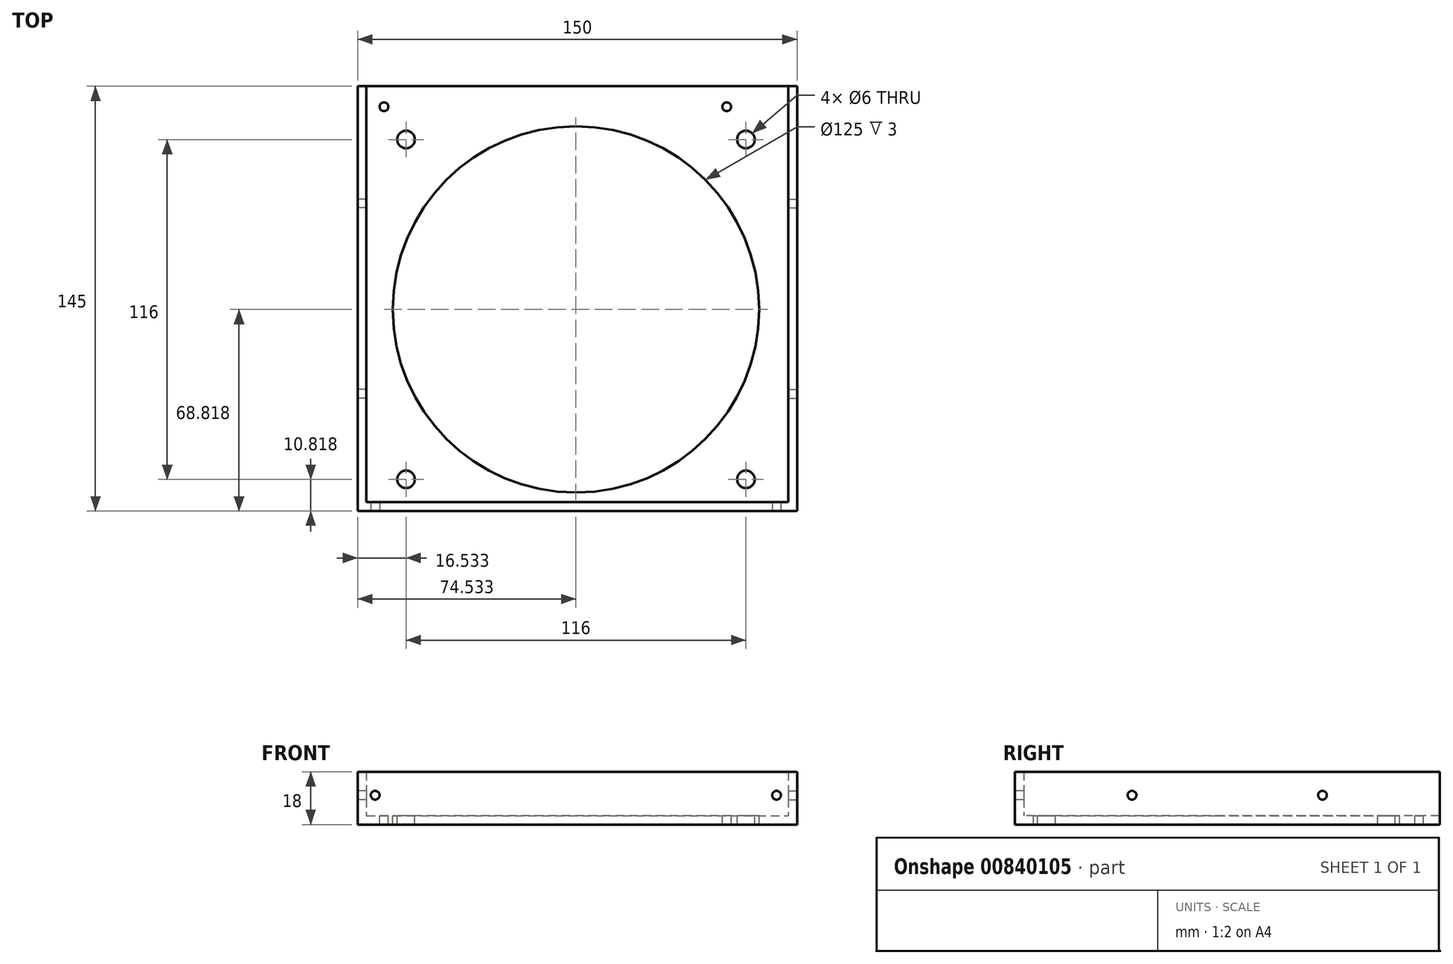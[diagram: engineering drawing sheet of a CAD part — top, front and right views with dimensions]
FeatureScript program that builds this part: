
annotation { "Feature Type Name" : "Feature", "Feature Type Description" : "" }
export const myFeature = defineFeature(function(context is Context, id is Id, definition is map)
    precondition{}
    {
        {
            var Q0;
            Q0=qCreatedBy(makeId("Top.planeOp"),FACE);
            var sketch = newSketch(context, id + "F0", { "sketchPlane" : qUnion([Q0])});
            skLineSegment(sketch, "E0.bottom", {"start": v(-58.92, 79.83) * mm, "end": v(91.08, 79.83) * mm});
            skLineSegment(sketch, "E0.top", {"start": v(-58.92, -65.17) * mm, "end": v(91.08, -65.17) * mm});
            skLineSegment(sketch, "E0.left", {"start": v(-58.92, 79.83) * mm, "end": v(-58.92, -65.17) * mm});
            skLineSegment(sketch, "E0.right", {"start": v(91.08, 79.83) * mm, "end": v(91.08, -65.17) * mm});
            skLineSegment(sketch, "E1", {"start": v(91.08, 79.83) * mm, "end": v(67.08, 79.83) * mm, "construction": true});
            skLineSegment(sketch, "E2", {"start": v(67.08, 79.83) * mm, "end": v(67.08, 72.83) * mm, "construction": true});
            skCircle(sketch, "E3", {"center": v(67.08, 72.83) * mm, "radius": 1.5 * mm});
            skLineSegment(sketch, "E4", {"start": v(-58.92, 79.83) * mm, "end": v(-49.92, 79.83) * mm, "construction": true});
            skLineSegment(sketch, "E5", {"start": v(-49.92, 79.83) * mm, "end": v(-49.92, 63.94) * mm, "construction": true});
            skCircle(sketch, "E6", {"center": v(-49.92, 72.83) * mm, "radius": 1.5 * mm});
            skLineSegment(sketch, "E7.bottom", {"start": v(-42.39, 61.65) * mm, "end": v(73.61, 61.65) * mm, "construction": true});
            skLineSegment(sketch, "E7.top", {"start": v(-42.39, -54.35) * mm, "end": v(73.61, -54.35) * mm, "construction": true});
            skLineSegment(sketch, "E7.left", {"start": v(-42.39, 61.65) * mm, "end": v(-42.39, -54.35) * mm, "construction": true});
            skLineSegment(sketch, "E7.right", {"start": v(73.61, 61.65) * mm, "end": v(73.61, -54.35) * mm, "construction": true});
            skLineSegment(sketch, "E8", {"start": v(-42.39, 61.65) * mm, "end": v(73.61, -54.35) * mm, "construction": true});
            skCircle(sketch, "E9", {"center": v(15.61, 3.65) * mm, "radius": 62.5 * mm});
            skCircle(sketch, "E10", {"center": v(-42.39, 61.65) * mm, "radius": 3 * mm});
            skCircle(sketch, "E11", {"center": v(-42.39, -54.35) * mm, "radius": 3 * mm});
            skCircle(sketch, "E12", {"center": v(73.61, -54.35) * mm, "radius": 3 * mm});
            skCircle(sketch, "E13", {"center": v(73.61, 61.65) * mm, "radius": 3 * mm});
            skLineSegment(sketch, "E14", {"start": v(-228.5, -70.16) * mm, "end": v(-428.5, -70.16) * mm});
            skLineSegment(sketch, "E15", {"start": v(-428.5, -70.16) * mm, "end": v(-428.5, 129.84) * mm});
            skLineSegment(sketch, "E16", {"start": v(-428.5, 129.84) * mm, "end": v(-228.5, -70.16) * mm});
            skLineSegment(sketch, "E17", {"start": v(-428.5, -70.16) * mm, "end": v(-425.5, -70.16) * mm});
            skLineSegment(sketch, "E18", {"start": v(-425.5, -70.16) * mm, "end": v(-425.5, 126.84) * mm});
            skLineSegment(sketch, "E19", {"start": v(-428.5, -70.16) * mm, "end": v(-428.5, -67.16) * mm});
            skLineSegment(sketch, "E20", {"start": v(-428.5, -67.16) * mm, "end": v(-231.5, -67.16) * mm});
            skLineSegment(sketch, "E21", {"start": v(-228.5, -70.16) * mm, "end": v(-232.75, -70.16) * mm});
            skLineSegment(sketch, "E22", {"start": v(-232.75, -70.16) * mm, "end": v(-428.5, 125.6) * mm});
            skLineSegment(sketch, "E23", {"start": v(-428.5, -70.16) * mm, "end": v(-330.63, 27.72) * mm});
            skLineSegment(sketch, "E24", {"start": v(-428.5, -67.16) * mm, "end": v(-332.13, 29.22) * mm});
            skLineSegment(sketch, "E25", {"start": v(-425.5, -70.16) * mm, "end": v(-329.13, 26.22) * mm});
            skLineSegment(sketch, "E26", {"start": v(-58.92, 79.83) * mm, "end": v(-55.92, 79.83) * mm, "construction": true});
            skLineSegment(sketch, "E27", {"start": v(-55.92, 79.83) * mm, "end": v(-55.92, -65.17) * mm});
            skLineSegment(sketch, "E28", {"start": v(-58.92, -65.17) * mm, "end": v(-58.92, -62.17) * mm, "construction": true});
            skLineSegment(sketch, "E29", {"start": v(-58.92, -62.17) * mm, "end": v(91.08, -62.17) * mm});
            skLineSegment(sketch, "E30", {"start": v(91.08, -65.17) * mm, "end": v(88.08, -65.17) * mm, "construction": true});
            skLineSegment(sketch, "E31", {"start": v(88.08, -65.17) * mm, "end": v(88.08, 79.83) * mm});
            skLineSegment(sketch, "E32", {"start": v(67.08, 72.83) * mm, "end": v(-65.04, 72.83) * mm, "construction": true});
            skSolve(sketch);
        }
        {
            var Q0;
            {var subQ0=sQuery(id+"F0.wireOp",EDGE,"E0.left");var subQ1=sQuery(id+"F0.wireOp",EDGE,"E0.bottom");var subQ2=makeQuery(id+"F0.imprint","INTERSECT",VERTEX,{"derivedFrom":[subQ1,subQ0]});Q0=makeQuery(id+"F0.imprint","IMPRINT",FACE,{"disambiguationData":[TD([[makeQuery(id+"F0.imprint","IMPRINT",EDGE,{"disambiguationData":[TD([[subQ2,-1.0]])],"derivedFrom":subQ1}),-1.0]])]});}
            var Q1;
            Q1=makeQuery(id+"F0.imprint","IMPRINT",FACE,{"disambiguationData":[TD([[makeQuery(id+"F0.imprint","IMPRINT",EDGE,{"derivedFrom":sQuery(id+"F0.wireOp",EDGE,"E3")}),-1.0]])]});
            var Q2;
            {var subQ0=sQuery(id+"F0.wireOp",EDGE,"E0.right");var subQ1=sQuery(id+"F0.wireOp",EDGE,"E0.bottom");var subQ2=makeQuery(id+"F0.imprint","INTERSECT",VERTEX,{"derivedFrom":[subQ1,subQ0]});Q2=makeQuery(id+"F0.imprint","IMPRINT",FACE,{"disambiguationData":[TD([[makeQuery(id+"F0.imprint","IMPRINT",EDGE,{"disambiguationData":[TD([[subQ2,1.0]])],"derivedFrom":subQ1}),-1.0]])]});}
            var Q3;
            {var subQ0=sQuery(id+"F0.wireOp",EDGE,"E27");var subQ1=sQuery(id+"F0.wireOp",EDGE,"E0.top");var subQ2=makeQuery(id+"F0.imprint","INTERSECT",VERTEX,{"derivedFrom":[subQ1,subQ0]});Q3=makeQuery(id+"F0.imprint","IMPRINT",FACE,{"disambiguationData":[TD([[makeQuery(id+"F0.imprint","IMPRINT",EDGE,{"disambiguationData":[TD([[subQ2,-1.0]])],"derivedFrom":subQ1}),1.0]])]});}
            var Q4;
            {var subQ0=sQuery(id+"F0.wireOp",EDGE,"E0.right");var subQ1=sQuery(id+"F0.wireOp",EDGE,"E0.top");var subQ2=makeQuery(id+"F0.imprint","INTERSECT",VERTEX,{"derivedFrom":[subQ1,subQ0]});Q4=makeQuery(id+"F0.imprint","IMPRINT",FACE,{"disambiguationData":[TD([[makeQuery(id+"F0.imprint","IMPRINT",EDGE,{"disambiguationData":[TD([[subQ2,1.0]])],"derivedFrom":subQ1}),1.0]])]});}
            var Q5;
            {var subQ0=sQuery(id+"F0.wireOp",EDGE,"E0.left");var subQ1=sQuery(id+"F0.wireOp",EDGE,"E0.top");var subQ2=makeQuery(id+"F0.imprint","INTERSECT",VERTEX,{"derivedFrom":[subQ1,subQ0]});Q5=makeQuery(id+"F0.imprint","IMPRINT",FACE,{"disambiguationData":[TD([[makeQuery(id+"F0.imprint","IMPRINT",EDGE,{"disambiguationData":[TD([[subQ2,-1.0]])],"derivedFrom":subQ1}),1.0]])]});}
            extrude(context, id + "F1", {"entities" : qUnion([Q0, Q1, Q2, Q3, Q4, Q5]), "oppositeDirection" : true, "depth" : 3 * mm, "offsetDistance" : 25 * mm});
        }
        {
            var Q0;
            {var subQ0=sQuery(id+"F0.wireOp",EDGE,"E0.left");var subQ1=sQuery(id+"F0.wireOp",EDGE,"E0.bottom");var subQ2=makeQuery(id+"F0.imprint","INTERSECT",VERTEX,{"derivedFrom":[subQ1,subQ0]});Q0=makeQuery(id+"F0.imprint","IMPRINT",FACE,{"disambiguationData":[TD([[makeQuery(id+"F0.imprint","IMPRINT",EDGE,{"disambiguationData":[TD([[subQ2,-1.0]])],"derivedFrom":subQ1}),-1.0]])]});}
            var Q1;
            {var subQ0=sQuery(id+"F0.wireOp",EDGE,"E0.left");var subQ1=sQuery(id+"F0.wireOp",EDGE,"E0.top");var subQ2=makeQuery(id+"F0.imprint","INTERSECT",VERTEX,{"derivedFrom":[subQ1,subQ0]});Q1=makeQuery(id+"F0.imprint","IMPRINT",FACE,{"disambiguationData":[TD([[makeQuery(id+"F0.imprint","IMPRINT",EDGE,{"disambiguationData":[TD([[subQ2,-1.0]])],"derivedFrom":subQ1}),1.0]])]});}
            var Q2;
            {var subQ0=sQuery(id+"F0.wireOp",EDGE,"E27");var subQ1=sQuery(id+"F0.wireOp",EDGE,"E0.top");var subQ2=makeQuery(id+"F0.imprint","INTERSECT",VERTEX,{"derivedFrom":[subQ1,subQ0]});Q2=makeQuery(id+"F0.imprint","IMPRINT",FACE,{"disambiguationData":[TD([[makeQuery(id+"F0.imprint","IMPRINT",EDGE,{"disambiguationData":[TD([[subQ2,-1.0]])],"derivedFrom":subQ1}),1.0]])]});}
            var Q3;
            {var subQ0=sQuery(id+"F0.wireOp",EDGE,"E0.right");var subQ1=sQuery(id+"F0.wireOp",EDGE,"E0.top");var subQ2=makeQuery(id+"F0.imprint","INTERSECT",VERTEX,{"derivedFrom":[subQ1,subQ0]});Q3=makeQuery(id+"F0.imprint","IMPRINT",FACE,{"disambiguationData":[TD([[makeQuery(id+"F0.imprint","IMPRINT",EDGE,{"disambiguationData":[TD([[subQ2,1.0]])],"derivedFrom":subQ1}),1.0]])]});}
            var Q4;
            {var subQ0=sQuery(id+"F0.wireOp",EDGE,"E0.right");var subQ1=sQuery(id+"F0.wireOp",EDGE,"E0.bottom");var subQ2=makeQuery(id+"F0.imprint","INTERSECT",VERTEX,{"derivedFrom":[subQ1,subQ0]});Q4=makeQuery(id+"F0.imprint","IMPRINT",FACE,{"disambiguationData":[TD([[makeQuery(id+"F0.imprint","IMPRINT",EDGE,{"disambiguationData":[TD([[subQ2,1.0]])],"derivedFrom":subQ1}),-1.0]])]});}
            extrude(context, id + "F2", {"entities" : qUnion([Q0, Q1, Q2, Q3, Q4]), "operationType" : NewBodyOperationType.ADD, "depth" : 15 * mm, "offsetDistance" : 25 * mm});
        }
        {
            var Q0;
            {var subQ0=sQuery(id+"F0.wireOp",EDGE,"E0.right");Q0=makeQuery(id+"F2.boolean.opBoolean","MERGE",FACE,{"derivedFrom":[makeQuery(id+"F1.opExtrude","SWEPT_FACE",FACE,{"disambiguationData":[OSD([subQ0])]}),makeQuery(id+"F2.opExtrude","SWEPT_FACE",FACE,{"disambiguationData":[OSD([subQ0])]})]});}
            var sketch = newSketch(context, id + "F3", { "sketchPlane" : qUnion([Q0])});
            skLineSegment(sketch, "E33", {"start": v(79.83, -3) * mm, "end": v(79.83, 7) * mm, "construction": true});
            skLineSegment(sketch, "E34", {"start": v(79.83, 7) * mm, "end": v(-65.17, 7) * mm, "construction": true});
            skCircle(sketch, "E35", {"center": v(39.83, 7) * mm, "radius": 1.5 * mm});
            skCircle(sketch, "E36", {"center": v(-25.17, 7) * mm, "radius": 1.5 * mm});
            skSolve(sketch);
        }
        {
            var Q0;
            {var subQ0=sQuery(id+"F0.wireOp",EDGE,"E0.top");Q0=makeQuery(id+"F2.boolean.opBoolean","MERGE",FACE,{"derivedFrom":[makeQuery(id+"F1.opExtrude","SWEPT_FACE",FACE,{"disambiguationData":[OSD([subQ0])]}),makeQuery(id+"F2.opExtrude","SWEPT_FACE",FACE,{"disambiguationData":[OSD([subQ0])]})]});}
            var sketch = newSketch(context, id + "F4", { "sketchPlane" : qUnion([Q0])});
            skLineSegment(sketch, "E37", {"start": v(91.08, -3) * mm, "end": v(91.08, 7) * mm, "construction": true});
            skLineSegment(sketch, "E38", {"start": v(91.08, 7) * mm, "end": v(-58.92, 7) * mm, "construction": true});
            skCircle(sketch, "E39", {"center": v(84.08, 7) * mm, "radius": 1.5 * mm});
            skCircle(sketch, "E40", {"center": v(-52.92, 7) * mm, "radius": 1.5 * mm});
            skSolve(sketch);
        }
        {
            var Q0;
            {var subQ0=sQuery(id+"F0.wireOp",EDGE,"E0.left");Q0=makeQuery(id+"F2.boolean.opBoolean","MERGE",FACE,{"derivedFrom":[makeQuery(id+"F1.opExtrude","SWEPT_FACE",FACE,{"disambiguationData":[OSD([subQ0])]}),makeQuery(id+"F2.opExtrude","SWEPT_FACE",FACE,{"disambiguationData":[OSD([subQ0])]})]});}
            var sketch = newSketch(context, id + "F5", { "sketchPlane" : qUnion([Q0])});
            skLineSegment(sketch, "E41", {"start": v(65.17, -3) * mm, "end": v(65.17, 7) * mm, "construction": true});
            skLineSegment(sketch, "E42", {"start": v(65.17, 7) * mm, "end": v(-79.83, 7) * mm, "construction": true});
            skCircle(sketch, "E43", {"center": v(25.17, 7) * mm, "radius": 1.5 * mm});
            skCircle(sketch, "E44", {"center": v(-39.83, 7) * mm, "radius": 1.5 * mm});
            skSolve(sketch);
        }
        {
            var Q0;
            Q0=makeQuery(id+"F5.imprint","IMPRINT",FACE,{"disambiguationData":[TD([[makeQuery(id+"F5.imprint","IMPRINT",EDGE,{"derivedFrom":sQuery(id+"F5.wireOp",EDGE,"E43")}),1.0]])]});
            var Q1;
            Q1=makeQuery(id+"F5.imprint","IMPRINT",FACE,{"disambiguationData":[TD([[makeQuery(id+"F5.imprint","IMPRINT",EDGE,{"derivedFrom":sQuery(id+"F5.wireOp",EDGE,"E44")}),1.0]])]});
            extrude(context, id + "F6", {"entities" : qUnion([Q0, Q1]), "operationType" : NewBodyOperationType.REMOVE, "oppositeDirection" : true, "depth" : 3 * mm, "offsetDistance" : 25 * mm});
        }
        {
            var Q0;
            Q0=makeQuery(id+"F4.imprint","IMPRINT",FACE,{"disambiguationData":[TD([[makeQuery(id+"F4.imprint","IMPRINT",EDGE,{"derivedFrom":sQuery(id+"F4.wireOp",EDGE,"E40")}),1.0]])]});
            var Q1;
            Q1=makeQuery(id+"F4.imprint","IMPRINT",FACE,{"disambiguationData":[TD([[makeQuery(id+"F4.imprint","IMPRINT",EDGE,{"derivedFrom":sQuery(id+"F4.wireOp",EDGE,"E39")}),1.0]])]});
            extrude(context, id + "F7", {"entities" : qUnion([Q0, Q1]), "operationType" : NewBodyOperationType.REMOVE, "oppositeDirection" : true, "depth" : 25 * mm, "offsetDistance" : 25 * mm});
        }
        {
            var Q0;
            Q0=makeQuery(id+"F3.imprint","IMPRINT",FACE,{"disambiguationData":[TD([[makeQuery(id+"F3.imprint","IMPRINT",EDGE,{"derivedFrom":sQuery(id+"F3.wireOp",EDGE,"E36")}),1.0]])]});
            var Q1;
            Q1=makeQuery(id+"F3.imprint","IMPRINT",FACE,{"disambiguationData":[TD([[makeQuery(id+"F3.imprint","IMPRINT",EDGE,{"derivedFrom":sQuery(id+"F3.wireOp",EDGE,"E35")}),1.0]])]});
            extrude(context, id + "F8", {"entities" : qUnion([Q0, Q1]), "operationType" : NewBodyOperationType.REMOVE, "oppositeDirection" : true, "depth" : 25 * mm, "offsetDistance" : 25 * mm});
        }
    });
